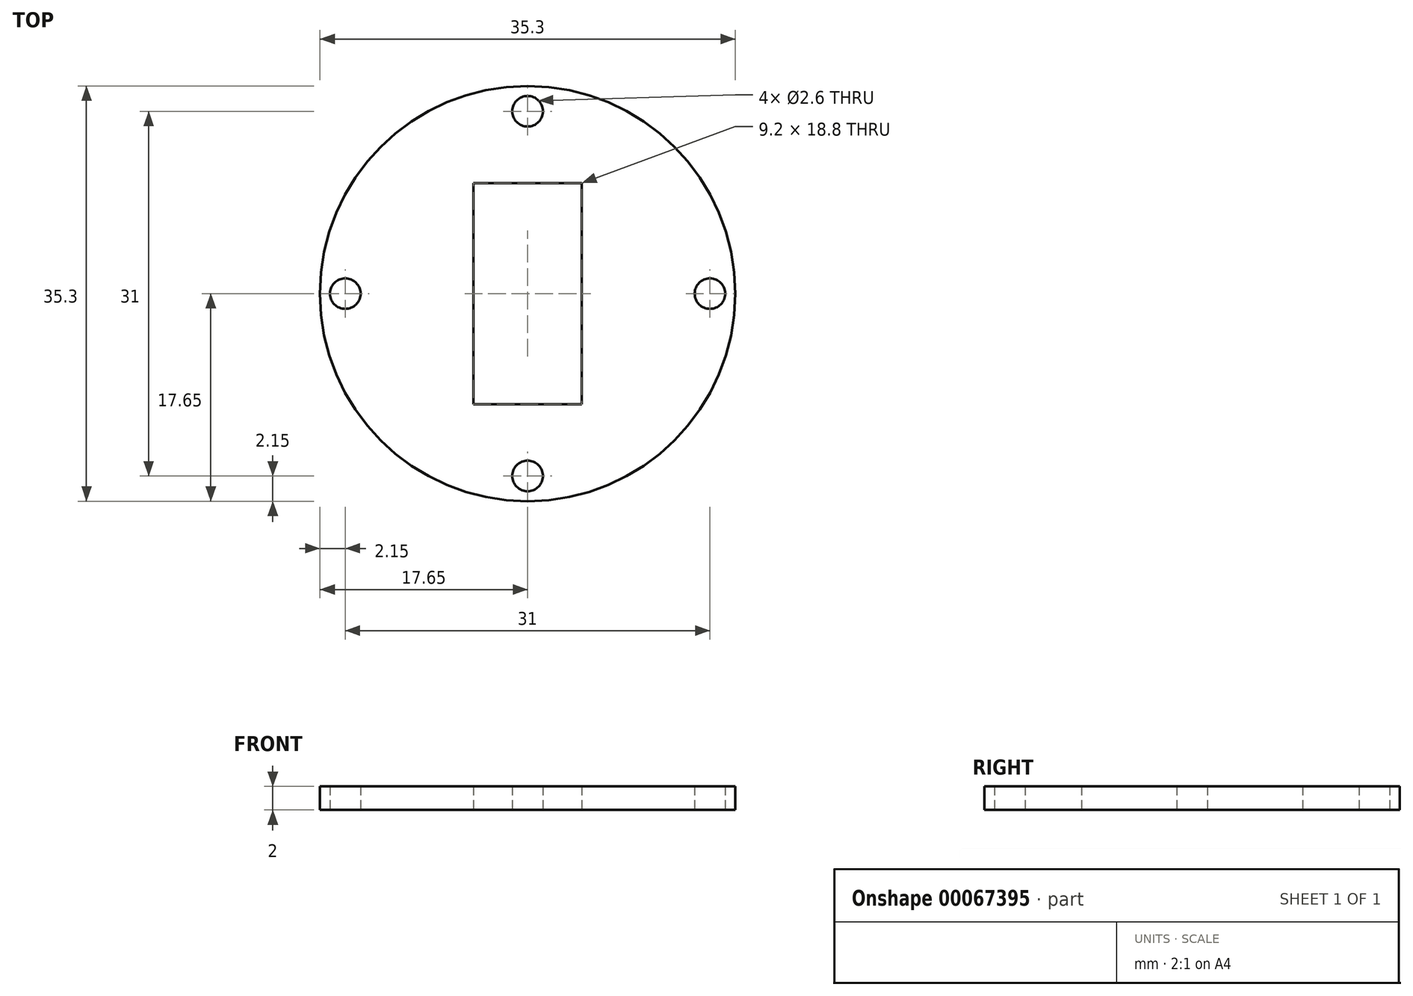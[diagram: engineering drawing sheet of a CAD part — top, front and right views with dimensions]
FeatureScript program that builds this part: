
annotation { "Feature Type Name" : "Feature", "Feature Type Description" : "" }
export const myFeature = defineFeature(function(context is Context, id is Id, definition is map)
    precondition{}
    {
        {
            var Q0;
            Q0=qCreatedBy(makeId("Top.planeOp"),FACE);
            var sketch = newSketch(context, id + "F0", { "sketchPlane" : qUnion([Q0])});
            skCircle(sketch, "E0", {"center": v(0, 0) * mm, "radius": 17.65 * mm});
            skLineSegment(sketch, "E1.bottom", {"start": v(-4.6, 9.4) * mm, "end": v(4.6, 9.4) * mm});
            skLineSegment(sketch, "E1.top", {"start": v(-4.6, -9.4) * mm, "end": v(4.6, -9.4) * mm});
            skLineSegment(sketch, "E1.left", {"start": v(-4.6, 9.4) * mm, "end": v(-4.6, -9.4) * mm});
            skLineSegment(sketch, "E1.right", {"start": v(4.6, 9.4) * mm, "end": v(4.6, -9.4) * mm});
            skCircle(sketch, "E2", {"center": v(0, 15.5) * mm, "radius": 1.3 * mm});
            skCircle(sketch, "E3", {"center": v(0, -15.5) * mm, "radius": 1.3 * mm});
            skCircle(sketch, "E4", {"center": v(15.5, 0) * mm, "radius": 1.3 * mm});
            skCircle(sketch, "E5", {"center": v(-15.5, 0) * mm, "radius": 1.3 * mm});
            skSolve(sketch);
        }
        {
            var Q0;
            Q0 = qSketchRegion(id + "F0", true);
            extrude(context, id + "F1", {"entities" : qUnion([Q0]), "depth" : 2 * mm});
        }
    });
